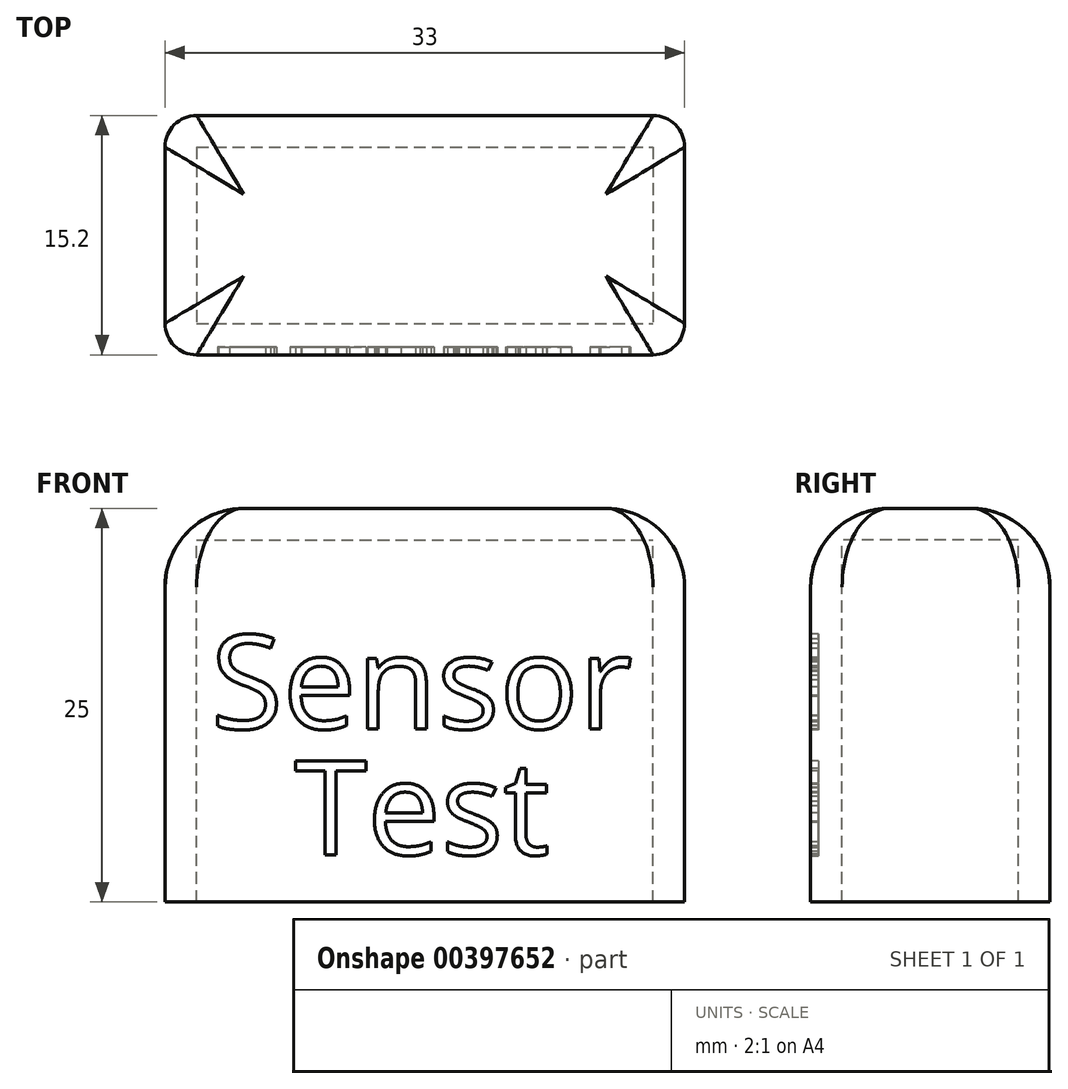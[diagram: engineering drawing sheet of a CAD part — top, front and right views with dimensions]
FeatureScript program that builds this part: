
annotation { "Feature Type Name" : "Feature", "Feature Type Description" : "" }
export const myFeature = defineFeature(function(context is Context, id is Id, definition is map)
    precondition{}
    {
        {
            var Q0;
            Q0=qCreatedBy(makeId("Top.planeOp"),FACE);
            var sketch = newSketch(context, id + "F0", { "sketchPlane" : qUnion([Q0])});
            skLineSegment(sketch, "E0.bottom", {"start": v(0, 0) * mm, "end": v(33, 0) * mm});
            skLineSegment(sketch, "E0.top", {"start": v(0, 15.2) * mm, "end": v(33, 15.2) * mm});
            skLineSegment(sketch, "E0.left", {"start": v(0, 0) * mm, "end": v(0, 15.2) * mm});
            skLineSegment(sketch, "E0.right", {"start": v(33, 0) * mm, "end": v(33, 15.2) * mm});
            skSolve(sketch);
        }
        {
            var Q0;
            Q0 = qSketchRegion(id + "F0", true);
            extrude(context, id + "F1", {"entities" : qUnion([Q0]), "depth" : 25 * mm});
        }
        {
            var Q0;
            Q0=makeQuery(id+"F1.opExtrude","CAP_FACE",FACE,{"disambiguationData":[OSD([sQuery(id+"F0.wireOp",EDGE,"E0.bottom"),sQuery(id+"F0.wireOp",EDGE,"E0.top"),sQuery(id+"F0.wireOp",EDGE,"E0.left"),sQuery(id+"F0.wireOp",EDGE,"E0.right")])],"isStart":false});
            shell(context, id + "F2", {"entities" : qUnion([Q0]), "thickness" : 2 * mm});
        }
        {
            var Q0;
            Q0=makeQuery(id+"F1.opExtrude","SWEPT_EDGE",EDGE,{"disambiguationData":[OSD([sQuery(id+"F0.wireOp",EDGE,"E0.bottom"),sQuery(id+"F0.wireOp",EDGE,"E0.left")])]});
            var Q1;
            Q1=makeQuery(id+"F1.opExtrude","SWEPT_EDGE",EDGE,{"disambiguationData":[OSD([sQuery(id+"F0.wireOp",EDGE,"E0.top"),sQuery(id+"F0.wireOp",EDGE,"E0.left")])]});
            var Q2;
            Q2=makeQuery(id+"F1.opExtrude","SWEPT_EDGE",EDGE,{"disambiguationData":[OSD([sQuery(id+"F0.wireOp",EDGE,"E0.bottom"),sQuery(id+"F0.wireOp",EDGE,"E0.right")])]});
            var Q3;
            Q3=makeQuery(id+"F1.opExtrude","SWEPT_EDGE",EDGE,{"disambiguationData":[OSD([sQuery(id+"F0.wireOp",EDGE,"E0.top"),sQuery(id+"F0.wireOp",EDGE,"E0.right")])]});
            fillet(context, id + "F3", {"entities" : qUnion([Q0, Q1, Q2, Q3]), "radius" : 2 * mm, "tangentPropagation" : true, "allowEdgeOverflow" : false});
        }
        {
            var Q0;
            Q0=makeQuery(id+"F1.opExtrude","CAP_FACE",FACE,{"disambiguationData":[OSD([sQuery(id+"F0.wireOp",EDGE,"E0.bottom"),sQuery(id+"F0.wireOp",EDGE,"E0.top"),sQuery(id+"F0.wireOp",EDGE,"E0.left"),sQuery(id+"F0.wireOp",EDGE,"E0.right")])],"isStart":true});
            fillet(context, id + "F4", {"entities" : qUnion([Q0]), "radius" : 5 * mm, "tangentPropagation" : true, "allowEdgeOverflow" : false});
        }
        {
            var Q0;
            Q0=makeQuery(id+"F1.opExtrude","SWEPT_BODY",BODY,{"disambiguationData":[OSD([sQuery(id+"F0.wireOp",EDGE,"E0.bottom"),sQuery(id+"F0.wireOp",EDGE,"E0.top"),sQuery(id+"F0.wireOp",EDGE,"E0.left"),sQuery(id+"F0.wireOp",EDGE,"E0.right")])]});
            var Q1;
            Q1=makeQuery(id+"F1.opExtrude","CAP_EDGE",EDGE,{"disambiguationData":[OSD([sQuery(id+"F0.wireOp",EDGE,"E0.bottom")])],"isStart":false});
            transform(context, id + "F5", {"entities" : qUnion([Q0]), "transformType" : TransformType.ROTATION, "transformAxis" : qUnion([Q1]), "angle" : 180 * degree, "makeCopy" : false});
        }
        {
            var Q0;
            Q0=makeQuery(id+"F1.opExtrude","SWEPT_BODY",BODY,{"disambiguationData":[OSD([sQuery(id+"F0.wireOp",EDGE,"E0.bottom"),sQuery(id+"F0.wireOp",EDGE,"E0.top"),sQuery(id+"F0.wireOp",EDGE,"E0.left"),sQuery(id+"F0.wireOp",EDGE,"E0.right")])]});
            transform(context, id + "F6", {"entities" : qUnion([Q0]), "transformType" : TransformType.TRANSLATION_3D, "dx" : 0 * mm, "dy" : 0 * mm, "dz" : -25 * mm, "makeCopy" : false});
        }
        {
            var Q0;
            Q0=makeQuery(id+"F1.opExtrude","SWEPT_FACE",FACE,{"disambiguationData":[OSD([sQuery(id+"F0.wireOp",EDGE,"E0.top")])]});
            var sketch = newSketch(context, id + "F7", { "sketchPlane" : qUnion([Q0])});
            skText(sketch, "E1", { "text": "Test", "fontName": "OpenSans-Regular.ttf"});
            skText(sketch, "E2", { "text": "Sensor", "fontName": "OpenSans-Regular.ttf"});
            const initialGuessF7  = {"E1": [0.00822, 0.003, 1, 0, 0.006], "E2": [0.0029, 0.011, 1, 0, 0.006]};
            skSetInitialGuess(sketch, initialGuessF7);
            skSolve(sketch);
        }
        {
            var Q0;
            Q0 = qSketchRegion(id + "F7", true);
            extrude(context, id + "F8", {"entities" : qUnion([Q0]), "operationType" : NewBodyOperationType.REMOVE, "oppositeDirection" : true, "depth" : 0.5 * mm, "offsetDistance" : 25 * mm});
        }
    });
